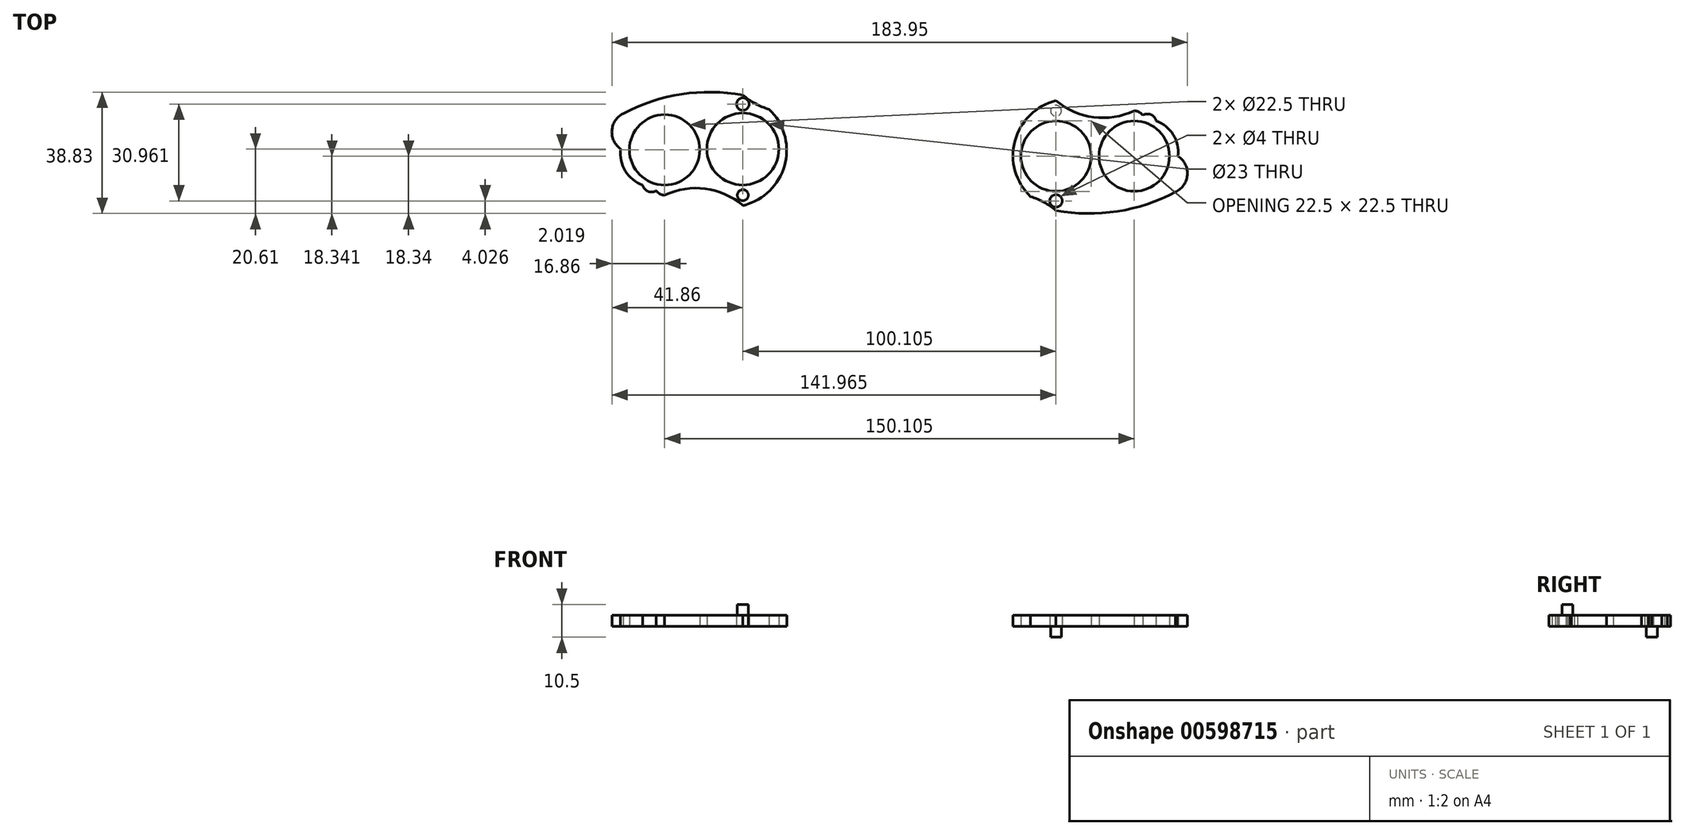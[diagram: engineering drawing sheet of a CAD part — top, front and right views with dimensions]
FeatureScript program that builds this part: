
annotation { "Feature Type Name" : "Feature", "Feature Type Description" : "" }
export const myFeature = defineFeature(function(context is Context, id is Id, definition is map)
    precondition{}
    {
        {
            var Q0;
            Q0=qCreatedBy(makeId("Top.planeOp"),FACE);
            var sketch = newSketch(context, id + "F0", { "sketchPlane" : qUnion([Q0])});
            skCircle(sketch, "E0", {"center": v(0, 0) * mm, "radius": 11.5 * mm});
            skPoint(sketch, "E1", {"position": v(-11.5, 0) * mm});
            skLineSegment(sketch, "E2", {"start": v(-11.5, 11.21) * mm, "end": v(-38.5, 11.21) * mm});
            skCircle(sketch, "E3", {"center": v(-25, -0.25) * mm, "radius": 11.25 * mm});
            skPoint(sketch, "E3.centerSnap0", {"position": v(-25, 11.21) * mm});
            skLineSegment(sketch, "E4", {"start": v(0, 0) * mm, "end": v(0, -5.7) * mm});
            skLineSegment(sketch, "E5", {"start": v(-25, -11.5) * mm, "end": v(-39, -11.5) * mm});
            skArc(sketch, "E6", {"start": v(-32, 11.21) * mm, "mid": v(-40.86, 8.95) * mm, "end": v(-39, 0) * mm});
            skPoint(sketch, "E6.startSnap0", {"position": v(-32, -11.5) * mm});
            skArc(sketch, "E7", {"start": v(0, 11.21) * mm, "mid": v(-19.25, 15.91) * mm, "end": v(-38.5, 11.21) * mm});
            skArc(sketch, "E8", {"start": v(-39, 0) * mm, "mid": v(-35.23, -9.68) * mm, "end": v(-25, -11.5) * mm});
            skCircle(sketch, "E9", {"center": v(-25, -11.5) * mm, "radius": 3.25 * mm});
            skArc(sketch, "E10", {"start": v(-32, -11.5) * mm, "mid": v(-30.34, -13.54) * mm, "end": v(-27.71, -13.3) * mm});
            skCircle(sketch, "E11", {"center": v(0, 14.38) * mm, "radius": 2.88 * mm});
            skArc(sketch, "E12", {"start": v(0, 17.26) * mm, "mid": v(-19.76, 17.5) * mm, "end": v(-38.5, 11.21) * mm});
            skCircle(sketch, "E13", {"center": v(0, 14.38) * mm, "radius": 2 * mm});
            skCircle(sketch, "E14", {"center": v(0, -14.75) * mm, "radius": 3.25 * mm});
            skArc(sketch, "E15", {"start": v(0, -18) * mm, "mid": v(-12.02, -12.7) * mm, "end": v(-25, -14.75) * mm});
            skCircle(sketch, "E16", {"center": v(0, -14.75) * mm, "radius": 1.75 * mm});
            skArc(sketch, "E17", {"start": v(0, -18) * mm, "mid": v(14.02, -0.37) * mm, "end": v(0, 17.26) * mm});
            skLineSegment(sketch, "E18", {"start": v(38.9, 0.03) * mm, "end": v(-39.1, 0.03) * mm});
            skPoint(sketch, "E19", {"position": v(-0.1, 0.03) * mm});
            skLineSegment(sketch, "E20", {"start": v(-25, -14.75) * mm, "end": v(0, -18) * mm});
            skLineSegment(sketch, "E21", {"start": v(0, -18) * mm, "end": v(-23.35, -18) * mm});
            skLineSegment(sketch, "E22", {"start": v(0, 17.26) * mm, "end": v(26.06, 17.26) * mm});
            skArc(sketch, "E23", {"start": v(0, 17.26) * mm, "mid": v(12.02, 11.95) * mm, "end": v(25, 14) * mm});
            skLineSegment(sketch, "E24", {"start": v(0, 17.26) * mm, "end": v(25, 14) * mm});
            skCircle(sketch, "E25", {"center": v(100.1, -2.27) * mm, "radius": 11.25 * mm});
            skPoint(sketch, "E26", {"position": v(111.35, -2.27) * mm});
            skLineSegment(sketch, "E27", {"start": v(111.35, -13.48) * mm, "end": v(138.85, -13.48) * mm});
            skCircle(sketch, "E28", {"center": v(125.1, -2.27) * mm, "radius": 11.25 * mm});
            skPoint(sketch, "E28.centerSnap0", {"position": v(125.1, -13.48) * mm});
            skLineSegment(sketch, "E29", {"start": v(100.1, -2.27) * mm, "end": v(100.1, 3.43) * mm});
            skLineSegment(sketch, "E30", {"start": v(125.1, 8.98) * mm, "end": v(139.1, 8.98) * mm});
            skArc(sketch, "E31", {"start": v(132.1, -13.48) * mm, "mid": v(141.09, -11.3) * mm, "end": v(139.1, -2.27) * mm});
            skPoint(sketch, "E31.startSnap0", {"position": v(132.1, 8.98) * mm});
            skArc(sketch, "E32", {"start": v(100.1, -13.48) * mm, "mid": v(119.48, -18.25) * mm, "end": v(138.85, -13.48) * mm});
            skArc(sketch, "E33", {"start": v(139.1, -2.27) * mm, "mid": v(135.23, 7.24) * mm, "end": v(125.1, 8.98) * mm});
            skCircle(sketch, "E34", {"center": v(125.1, 8.98) * mm, "radius": 3.25 * mm});
            skArc(sketch, "E35", {"start": v(132.1, 8.98) * mm, "mid": v(130.44, 11.02) * mm, "end": v(127.82, 10.77) * mm});
            skCircle(sketch, "E36", {"center": v(100.1, -16.58) * mm, "radius": 3.06 * mm});
            skArc(sketch, "E37", {"start": v(100.1, -19.65) * mm, "mid": v(120, -19.88) * mm, "end": v(138.85, -13.48) * mm});
            skCircle(sketch, "E38", {"center": v(100.1, -16.58) * mm, "radius": 2 * mm});
            skCircle(sketch, "E39", {"center": v(100.1, 12.23) * mm, "radius": 3.25 * mm});
            skArc(sketch, "E40", {"start": v(100.1, 15.48) * mm, "mid": v(112.13, 10.18) * mm, "end": v(125.1, 12.23) * mm});
            skCircle(sketch, "E41", {"center": v(100.1, 12.23) * mm, "radius": 1.75 * mm});
            skArc(sketch, "E42", {"start": v(100.1, 15.48) * mm, "mid": v(86.35, -2.08) * mm, "end": v(100.1, -19.65) * mm});
            skLineSegment(sketch, "E43", {"start": v(61.21, -2.3) * mm, "end": v(139.21, -2.3) * mm});
            skPoint(sketch, "E44", {"position": v(100.21, -2.3) * mm});
            skLineSegment(sketch, "E45", {"start": v(125.1, 12.23) * mm, "end": v(100.1, 15.48) * mm});
            skLineSegment(sketch, "E46", {"start": v(100.1, 15.48) * mm, "end": v(123.45, 15.48) * mm});
            skLineSegment(sketch, "E47", {"start": v(100.1, -19.65) * mm, "end": v(74.04, -19.65) * mm});
            skArc(sketch, "E48", {"start": v(100.1, -19.65) * mm, "mid": v(88.08, -14.34) * mm, "end": v(75.1, -16.4) * mm});
            skLineSegment(sketch, "E49", {"start": v(100.1, -19.65) * mm, "end": v(75.1, -16.4) * mm});
            skSolve(sketch);
        }
        {
            var Q0;
            {var subQ0=sQuery(id+"F0.wireOp",EDGE,"E12");var subQ1=sQuery(id+"F0.wireOp",EDGE,"E6");var subQ3=makeQuery(id+"F0.imprint","INTERSECT",VERTEX,{"derivedFrom":[subQ1,subQ0]});Q0=makeQuery(id+"F0.imprint","IMPRINT",FACE,{"disambiguationData":[TD([[makeQuery(id+"F0.imprint","IMPRINT",EDGE,{"disambiguationData":[TD([[subQ3,-1.0]])],"derivedFrom":subQ1}),1.0]])]});}
            var Q1;
            {var subQ0=sQuery(id+"F0.wireOp",EDGE,"E15");var subQ1=sQuery(id+"F0.wireOp",EDGE,"E9");var subQ2=makeQuery(id+"F0.imprint","INTERSECT",VERTEX,{"disambiguationData":[OD(0.0)],"derivedFrom":[subQ1,subQ0]});Q1=makeQuery(id+"F0.imprint","IMPRINT",FACE,{"disambiguationData":[TD([[makeQuery(id+"F0.imprint","IMPRINT",EDGE,{"disambiguationData":[TD([[subQ2,-1.0]])],"derivedFrom":subQ1}),1.0]])]});}
            var Q2;
            {var subQ0=sQuery(id+"F0.wireOp",EDGE,"E17");var subQ1=sQuery(id+"F0.wireOp",EDGE,"E14");var subQ3=makeQuery(id+"F0.imprint","INTERSECT",VERTEX,{"derivedFrom":[subQ1,subQ0]});Q2=makeQuery(id+"F0.imprint","IMPRINT",FACE,{"disambiguationData":[TD([[makeQuery(id+"F0.imprint","IMPRINT",EDGE,{"disambiguationData":[TD([[subQ3,1.0]])],"derivedFrom":subQ1}),1.0]])]});}
            var Q3;
            {var subQ1=sQuery(id+"F0.wireOp",EDGE,"E6");var subQ2=sQuery(id+"F0.wireOp",EDGE,"E2");var subQ4=makeQuery(id+"F0.imprint","INTERSECT",VERTEX,{"derivedFrom":[subQ2,subQ1]});Q3=makeQuery(id+"F0.imprint","IMPRINT",FACE,{"disambiguationData":[TD([[makeQuery(id+"F0.imprint","IMPRINT",EDGE,{"disambiguationData":[TD([[subQ4,-1.0]])],"derivedFrom":subQ1}),1.0]])]});}
            var Q4;
            {var subQ0=sQuery(id+"F0.wireOp",EDGE,"E10");Q4=makeQuery(id+"F0.imprint","IMPRINT",FACE,{"disambiguationData":[TD([[makeQuery(id+"F0.imprint","IMPRINT",EDGE,{"derivedFrom":subQ0}),1.0]])]});}
            var Q5;
            {var subQ0=sQuery(id+"F0.wireOp",EDGE,"E11");var subQ1=sQuery(id+"F0.wireOp",EDGE,"E0");var subQ2=makeQuery(id+"F0.imprint","INTERSECT",VERTEX,{"derivedFrom":[subQ1,subQ0]});Q5=makeQuery(id+"F0.imprint","IMPRINT",FACE,{"disambiguationData":[TD([[makeQuery(id+"F0.imprint","IMPRINT",EDGE,{"disambiguationData":[TD([[subQ2,1.0]])],"derivedFrom":subQ1}),-1.0]])]});}
            var Q6;
            {var subQ0=sQuery(id+"F0.wireOp",EDGE,"Woyptmnj-qtCU-fI4K-3zEF-vQYEEQSbvC8r");var subQ1=sQuery(id+"F0.wireOp",EDGE,"E0");var subQ2=makeQuery(id+"F0.imprint","INTERSECT",VERTEX,{"disambiguationData":[OD(0.0)],"derivedFrom":[subQ1,subQ0]});Q6=makeQuery(id+"F0.imprint","IMPRINT",FACE,{"disambiguationData":[TD([[makeQuery(id+"F0.imprint","IMPRINT",EDGE,{"disambiguationData":[TD([[subQ2,1.0]])],"derivedFrom":subQ1}),-1.0]])]});}
            var Q7;
            {var subQ1=sQuery(id+"F0.wireOp",EDGE,"E5");var subQ3=sQuery(id+"F0.wireOp",EDGE,"E9");var subQ4=makeQuery(id+"F0.imprint","INTERSECT",VERTEX,{"derivedFrom":[subQ1,subQ3]});Q7=makeQuery(id+"F0.imprint","IMPRINT",FACE,{"disambiguationData":[TD([[makeQuery(id+"F0.imprint","IMPRINT",EDGE,{"disambiguationData":[TD([[subQ4,-1.0]])],"derivedFrom":subQ3}),-1.0]])]});}
            var Q8;
            {var subQ0=sQuery(id+"F0.wireOp",EDGE,"E12");var subQ1=sQuery(id+"F0.wireOp",EDGE,"E6");var subQ2=makeQuery(id+"F0.imprint","INTERSECT",VERTEX,{"derivedFrom":[subQ1,subQ0]});Q8=makeQuery(id+"F0.imprint","IMPRINT",FACE,{"disambiguationData":[TD([[makeQuery(id+"F0.imprint","IMPRINT",EDGE,{"disambiguationData":[TD([[subQ2,1.0]])],"derivedFrom":subQ1}),-1.0]])]});}
            var Q9;
            {var subQ0=sQuery(id+"F0.wireOp",EDGE,"E12");var subQ1=sQuery(id+"F0.wireOp",EDGE,"E6");var subQ2=makeQuery(id+"F0.imprint","INTERSECT",VERTEX,{"derivedFrom":[subQ1,subQ0]});Q9=makeQuery(id+"F0.imprint","IMPRINT",FACE,{"disambiguationData":[TD([[makeQuery(id+"F0.imprint","IMPRINT",EDGE,{"disambiguationData":[TD([[subQ2,1.0]])],"derivedFrom":subQ1}),1.0]])]});}
            var Q10;
            {var subQ5=sQuery(id+"F0.wireOp",EDGE,"E3");var subQ7=sQuery(id+"F0.wireOp",EDGE,"Woyptmnj-qtCU-fI4K-3zEF-vQYEEQSbvC8r");var subQ8=makeQuery(id+"F0.imprint","INTERSECT",VERTEX,{"disambiguationData":[OD(0.0)],"derivedFrom":[subQ7,subQ5]});Q10=makeQuery(id+"F0.imprint","IMPRINT",FACE,{"disambiguationData":[TD([[makeQuery(id+"F0.imprint","IMPRINT",EDGE,{"disambiguationData":[TD([[subQ8,-1.0]])],"derivedFrom":subQ5}),-1.0]])]});}
            var Q11;
            {var subQ5=sQuery(id+"F0.wireOp",EDGE,"Woyptmnj-qtCU-fI4K-3zEF-vQYEEQSbvC8r");var subQ7=sQuery(id+"F0.wireOp",EDGE,"E0");var subQ8=makeQuery(id+"F0.imprint","INTERSECT",VERTEX,{"disambiguationData":[OD(1.0)],"derivedFrom":[subQ7,subQ5]});Q11=makeQuery(id+"F0.imprint","IMPRINT",FACE,{"disambiguationData":[TD([[makeQuery(id+"F0.imprint","IMPRINT",EDGE,{"disambiguationData":[TD([[subQ8,-1.0]])],"derivedFrom":subQ7}),-1.0]])]});}
            var Q12;
            {var subQ0=sQuery(id+"F0.wireOp",EDGE,"E9");var subQ1=makeQuery(id+"F0.imprint","INTERSECT",VERTEX,{"derivedFrom":[subQ0,sQuery(id+"F0.wireOp",EDGE,"E10")]});Q12=makeQuery(id+"F0.imprint","IMPRINT",FACE,{"disambiguationData":[TD([[makeQuery(id+"F0.imprint","IMPRINT",EDGE,{"disambiguationData":[TD([[subQ1,1.0]])],"derivedFrom":subQ0}),1.0]])]});}
            var Q13;
            Q13=makeQuery(id+"F0.imprint","IMPRINT",FACE,{"disambiguationData":[TD([[makeQuery(id+"F0.imprint","IMPRINT",EDGE,{"derivedFrom":sQuery(id+"F0.wireOp",EDGE,"E16")}),-1.0]])]});
            var Q14;
            {var subQ9=sQuery(id+"F0.wireOp",EDGE,"E11");var subQ11=sQuery(id+"F0.wireOp",EDGE,"E0");var subQ12=makeQuery(id+"F0.imprint","INTERSECT",VERTEX,{"derivedFrom":[subQ11,subQ9]});Q14=makeQuery(id+"F0.imprint","IMPRINT",FACE,{"disambiguationData":[TD([[makeQuery(id+"F0.imprint","IMPRINT",EDGE,{"disambiguationData":[TD([[subQ12,-1.0]])],"derivedFrom":subQ11}),-1.0]])]});}
            var Q15;
            {var subQ1=sQuery(id+"F0.wireOp",EDGE,"E5");var subQ3=sQuery(id+"F0.wireOp",EDGE,"E9");var subQ4=makeQuery(id+"F0.imprint","INTERSECT",VERTEX,{"derivedFrom":[subQ1,subQ3]});Q15=makeQuery(id+"F0.imprint","IMPRINT",FACE,{"disambiguationData":[TD([[makeQuery(id+"F0.imprint","IMPRINT",EDGE,{"disambiguationData":[TD([[subQ4,-1.0]])],"derivedFrom":subQ3}),1.0]])]});}
            var Q16;
            {var subQ1=sQuery(id+"F0.wireOp",EDGE,"E3");var subQ3=sQuery(id+"F0.wireOp",EDGE,"E9");var subQ4=makeQuery(id+"F0.imprint","INTERSECT",VERTEX,{"disambiguationData":[OD(0.0)],"derivedFrom":[subQ1,subQ3]});Q16=makeQuery(id+"F0.imprint","IMPRINT",FACE,{"disambiguationData":[TD([[makeQuery(id+"F0.imprint","IMPRINT",EDGE,{"disambiguationData":[TD([[subQ4,-1.0]])],"derivedFrom":subQ3}),1.0]])]});}
            var Q17;
            {var subQ6=sQuery(id+"F0.wireOp",EDGE,"E0");var subQ9=sQuery(id+"F0.wireOp",EDGE,"E18");var subQ11=makeQuery(id+"F0.imprint","INTERSECT",VERTEX,{"disambiguationData":[OD(1.0)],"derivedFrom":[subQ6,subQ9]});Q17=makeQuery(id+"F0.imprint","IMPRINT",FACE,{"disambiguationData":[TD([[makeQuery(id+"F0.imprint","IMPRINT",EDGE,{"disambiguationData":[TD([[subQ11,-1.0]])],"derivedFrom":subQ6}),-1.0]])]});}
            var Q18;
            {var subQ0=sQuery(id+"F0.wireOp",EDGE,"E18");var subQ1=sQuery(id+"F0.wireOp",EDGE,"E0");var subQ2=makeQuery(id+"F0.imprint","INTERSECT",VERTEX,{"disambiguationData":[OD(0.0)],"derivedFrom":[subQ1,subQ0]});Q18=makeQuery(id+"F0.imprint","IMPRINT",FACE,{"disambiguationData":[TD([[makeQuery(id+"F0.imprint","IMPRINT",EDGE,{"disambiguationData":[TD([[subQ2,1.0]])],"derivedFrom":subQ1}),-1.0]])]});}
            var Q19;
            {var subQ5=sQuery(id+"F0.wireOp",EDGE,"E18");var subQ9=sQuery(id+"F0.wireOp",EDGE,"E3");var subQ10=makeQuery(id+"F0.imprint","INTERSECT",VERTEX,{"disambiguationData":[OD(0.0)],"derivedFrom":[subQ9,subQ5]});Q19=makeQuery(id+"F0.imprint","IMPRINT",FACE,{"disambiguationData":[TD([[makeQuery(id+"F0.imprint","IMPRINT",EDGE,{"disambiguationData":[TD([[subQ10,-1.0]])],"derivedFrom":subQ9}),-1.0]])]});}
            var Q20;
            Q20=makeQuery(id+"F0.imprint","IMPRINT",FACE,{"disambiguationData":[TD([[makeQuery(id+"F0.imprint","IMPRINT",EDGE,{"derivedFrom":sQuery(id+"F0.wireOp",EDGE,"E13")}),-1.0]])]});
            var Q21;
            {var subQ0=sQuery(id+"F0.wireOp",EDGE,"E6");var subQ1=sQuery(id+"F0.wireOp",EDGE,"E2");var subQ8=makeQuery(id+"F0.imprint","INTERSECT",VERTEX,{"derivedFrom":[subQ1,subQ0]});Q21=makeQuery(id+"F0.imprint","IMPRINT",FACE,{"disambiguationData":[TD([[makeQuery(id+"F0.imprint","IMPRINT",EDGE,{"disambiguationData":[TD([[subQ8,1.0]])],"derivedFrom":subQ1}),1.0]])]});}
            var Q22;
            {var subQ5=sQuery(id+"F0.wireOp",EDGE,"E18");var subQ9=sQuery(id+"F0.wireOp",EDGE,"E3");var subQ10=makeQuery(id+"F0.imprint","INTERSECT",VERTEX,{"disambiguationData":[OD(1.0)],"derivedFrom":[subQ9,subQ5]});Q22=makeQuery(id+"F0.imprint","IMPRINT",FACE,{"disambiguationData":[TD([[makeQuery(id+"F0.imprint","IMPRINT",EDGE,{"disambiguationData":[TD([[subQ10,-1.0]])],"derivedFrom":subQ9}),-1.0]])]});}
            var Q23;
            {var subQ0=sQuery(id+"F0.wireOp",EDGE,"E11");var subQ1=sQuery(id+"F0.wireOp",EDGE,"E7");var subQ2=makeQuery(id+"F0.imprint","INTERSECT",VERTEX,{"disambiguationData":[OD(0.0)],"derivedFrom":[subQ1,subQ0]});Q23=makeQuery(id+"F0.imprint","IMPRINT",FACE,{"disambiguationData":[TD([[makeQuery(id+"F0.imprint","IMPRINT",EDGE,{"disambiguationData":[TD([[subQ2,-1.0]])],"derivedFrom":subQ1}),1.0]])]});}
            extrude(context, id + "F1", {"entities" : qUnion([Q0, Q1, Q2, Q3, Q4, Q5, Q6, Q7, Q8, Q9, Q10, Q11, Q12, Q13, Q14, Q15, Q16, Q17, Q18, Q19, Q20, Q21, Q22, Q23]), "depth" : 3.5 * mm, "offsetDistance" : 25 * mm});
        }
        {
            var Q0;
            Q0=makeQuery(id+"F0.imprint","IMPRINT",FACE,{"disambiguationData":[TD([[makeQuery(id+"F0.imprint","IMPRINT",EDGE,{"derivedFrom":sQuery(id+"F0.wireOp",EDGE,"E16")}),1.0]])]});
            extrude(context, id + "F2", {"entities" : qUnion([Q0]), "operationType" : NewBodyOperationType.ADD, "depth" : 7 * mm, "offsetDistance" : 25 * mm});
        }
        {
            var Q0;
            {var subQ0=sQuery(id+"F0.wireOp",EDGE,"E43");var subQ1=sQuery(id+"F0.wireOp",EDGE,"E25");var subQ2=makeQuery(id+"F0.imprint","INTERSECT",VERTEX,{"disambiguationData":[OD(0.0)],"derivedFrom":[subQ1,subQ0]});Q0=makeQuery(id+"F0.imprint","IMPRINT",FACE,{"disambiguationData":[TD([[makeQuery(id+"F0.imprint","IMPRINT",EDGE,{"disambiguationData":[TD([[subQ2,1.0]])],"derivedFrom":subQ1}),-1.0]])]});}
            var Q1;
            Q1=makeQuery(id+"F0.imprint","IMPRINT",FACE,{"disambiguationData":[TD([[makeQuery(id+"F0.imprint","IMPRINT",EDGE,{"derivedFrom":sQuery(id+"F0.wireOp",EDGE,"E41")}),-1.0]])]});
            var Q2;
            {var subQ1=sQuery(id+"F0.wireOp",EDGE,"E25");var subQ5=sQuery(id+"F0.wireOp",EDGE,"E43");var subQ10=makeQuery(id+"F0.imprint","INTERSECT",VERTEX,{"disambiguationData":[OD(1.0)],"derivedFrom":[subQ1,subQ5]});Q2=makeQuery(id+"F0.imprint","IMPRINT",FACE,{"disambiguationData":[TD([[makeQuery(id+"F0.imprint","IMPRINT",EDGE,{"disambiguationData":[TD([[subQ10,-1.0]])],"derivedFrom":subQ1}),-1.0]])]});}
            var Q3;
            {var subQ0=sQuery(id+"F0.wireOp",EDGE,"E37");var subQ1=sQuery(id+"F0.wireOp",EDGE,"E31");var subQ2=makeQuery(id+"F0.imprint","INTERSECT",VERTEX,{"derivedFrom":[subQ1,subQ0]});Q3=makeQuery(id+"F0.imprint","IMPRINT",FACE,{"disambiguationData":[TD([[makeQuery(id+"F0.imprint","IMPRINT",EDGE,{"disambiguationData":[TD([[subQ2,1.0]])],"derivedFrom":subQ1}),-1.0]])]});}
            var Q4;
            Q4=makeQuery(id+"F0.imprint","IMPRINT",FACE,{"disambiguationData":[TD([[makeQuery(id+"F0.imprint","IMPRINT",EDGE,{"derivedFrom":sQuery(id+"F0.wireOp",EDGE,"E38")}),-1.0]])]});
            var Q5;
            {var subQ7=sQuery(id+"F0.wireOp",EDGE,"E32");var subQ10=sQuery(id+"F0.wireOp",EDGE,"E25");var subQ15=makeQuery(id+"F0.imprint","INTERSECT",VERTEX,{"derivedFrom":[subQ10,subQ7]});Q5=makeQuery(id+"F0.imprint","IMPRINT",FACE,{"disambiguationData":[TD([[makeQuery(id+"F0.imprint","IMPRINT",EDGE,{"disambiguationData":[TD([[subQ15,-1.0]])],"derivedFrom":subQ10}),-1.0]])]});}
            var Q6;
            {var subQ0=sQuery(id+"F0.wireOp",EDGE,"E36");var subQ1=sQuery(id+"F0.wireOp",EDGE,"E32");var subQ2=makeQuery(id+"F0.imprint","INTERSECT",VERTEX,{"disambiguationData":[OD(0.0)],"derivedFrom":[subQ1,subQ0]});Q6=makeQuery(id+"F0.imprint","IMPRINT",FACE,{"disambiguationData":[TD([[makeQuery(id+"F0.imprint","IMPRINT",EDGE,{"disambiguationData":[TD([[subQ2,-1.0]])],"derivedFrom":subQ1}),1.0]])]});}
            var Q7;
            {var subQ3=sQuery(id+"F0.wireOp",EDGE,"E25");var subQ7=sQuery(id+"F0.wireOp",EDGE,"E36");var subQ9=makeQuery(id+"F0.imprint","INTERSECT",VERTEX,{"derivedFrom":[subQ3,subQ7]});Q7=makeQuery(id+"F0.imprint","IMPRINT",FACE,{"disambiguationData":[TD([[makeQuery(id+"F0.imprint","IMPRINT",EDGE,{"disambiguationData":[TD([[subQ9,1.0]])],"derivedFrom":subQ3}),-1.0]])]});}
            var Q8;
            {var subQ0=sQuery(id+"F0.wireOp",EDGE,"E34");var subQ1=makeQuery(id+"F0.imprint","INTERSECT",VERTEX,{"derivedFrom":[subQ0,sQuery(id+"F0.wireOp",EDGE,"E35")]});Q8=makeQuery(id+"F0.imprint","IMPRINT",FACE,{"disambiguationData":[TD([[makeQuery(id+"F0.imprint","IMPRINT",EDGE,{"disambiguationData":[TD([[subQ1,1.0]])],"derivedFrom":subQ0}),1.0]])]});}
            var Q9;
            {var subQ0=sQuery(id+"F0.wireOp",EDGE,"E35");Q9=makeQuery(id+"F0.imprint","IMPRINT",FACE,{"disambiguationData":[TD([[makeQuery(id+"F0.imprint","IMPRINT",EDGE,{"derivedFrom":subQ0}),1.0]])]});}
            var Q10;
            {var subQ5=sQuery(id+"F0.wireOp",EDGE,"E43");var subQ7=sQuery(id+"F0.wireOp",EDGE,"E28");var subQ8=makeQuery(id+"F0.imprint","INTERSECT",VERTEX,{"disambiguationData":[OD(1.0)],"derivedFrom":[subQ7,subQ5]});Q10=makeQuery(id+"F0.imprint","IMPRINT",FACE,{"disambiguationData":[TD([[makeQuery(id+"F0.imprint","IMPRINT",EDGE,{"disambiguationData":[TD([[subQ8,-1.0]])],"derivedFrom":subQ7}),-1.0]])]});}
            var Q11;
            {var subQ1=sQuery(id+"F0.wireOp",EDGE,"E30");var subQ3=sQuery(id+"F0.wireOp",EDGE,"E34");var subQ4=makeQuery(id+"F0.imprint","INTERSECT",VERTEX,{"derivedFrom":[subQ1,subQ3]});Q11=makeQuery(id+"F0.imprint","IMPRINT",FACE,{"disambiguationData":[TD([[makeQuery(id+"F0.imprint","IMPRINT",EDGE,{"disambiguationData":[TD([[subQ4,-1.0]])],"derivedFrom":subQ3}),-1.0]])]});}
            var Q12;
            {var subQ1=sQuery(id+"F0.wireOp",EDGE,"E30");var subQ3=sQuery(id+"F0.wireOp",EDGE,"E34");var subQ4=makeQuery(id+"F0.imprint","INTERSECT",VERTEX,{"derivedFrom":[subQ1,subQ3]});Q12=makeQuery(id+"F0.imprint","IMPRINT",FACE,{"disambiguationData":[TD([[makeQuery(id+"F0.imprint","IMPRINT",EDGE,{"disambiguationData":[TD([[subQ4,-1.0]])],"derivedFrom":subQ3}),1.0]])]});}
            var Q13;
            {var subQ1=sQuery(id+"F0.wireOp",EDGE,"E28");var subQ3=sQuery(id+"F0.wireOp",EDGE,"E34");var subQ4=makeQuery(id+"F0.imprint","INTERSECT",VERTEX,{"disambiguationData":[OD(0.0)],"derivedFrom":[subQ1,subQ3]});Q13=makeQuery(id+"F0.imprint","IMPRINT",FACE,{"disambiguationData":[TD([[makeQuery(id+"F0.imprint","IMPRINT",EDGE,{"disambiguationData":[TD([[subQ4,-1.0]])],"derivedFrom":subQ3}),1.0]])]});}
            var Q14;
            {var subQ0=sQuery(id+"F0.wireOp",EDGE,"E31");var subQ1=sQuery(id+"F0.wireOp",EDGE,"E27");var subQ8=makeQuery(id+"F0.imprint","INTERSECT",VERTEX,{"derivedFrom":[subQ1,subQ0]});Q14=makeQuery(id+"F0.imprint","IMPRINT",FACE,{"disambiguationData":[TD([[makeQuery(id+"F0.imprint","IMPRINT",EDGE,{"disambiguationData":[TD([[subQ8,1.0]])],"derivedFrom":subQ1}),1.0]])]});}
            var Q15;
            {var subQ1=sQuery(id+"F0.wireOp",EDGE,"E31");var subQ2=sQuery(id+"F0.wireOp",EDGE,"E27");var subQ4=makeQuery(id+"F0.imprint","INTERSECT",VERTEX,{"derivedFrom":[subQ2,subQ1]});Q15=makeQuery(id+"F0.imprint","IMPRINT",FACE,{"disambiguationData":[TD([[makeQuery(id+"F0.imprint","IMPRINT",EDGE,{"disambiguationData":[TD([[subQ4,-1.0]])],"derivedFrom":subQ1}),1.0]])]});}
            extrude(context, id + "F3", {"entities" : qUnion([Q0, Q1, Q2, Q3, Q4, Q5, Q6, Q7, Q8, Q9, Q10, Q11, Q12, Q13, Q14, Q15]), "depth" : 3.5 * mm, "offsetDistance" : 25 * mm});
        }
        {
            var Q0;
            Q0=makeQuery(id+"F0.imprint","IMPRINT",FACE,{"disambiguationData":[TD([[makeQuery(id+"F0.imprint","IMPRINT",EDGE,{"derivedFrom":sQuery(id+"F0.wireOp",EDGE,"E41")}),1.0]])]});
            extrude(context, id + "F4", {"entities" : qUnion([Q0]), "operationType" : NewBodyOperationType.ADD, "depth" : 3.5 * mm, "offsetDistance" : 25 * mm, "hasSecondDirection" : true, "secondDirectionOppositeDirection" : true, "secondDirectionDepth" : 3.5 * mm});
        }
    });
